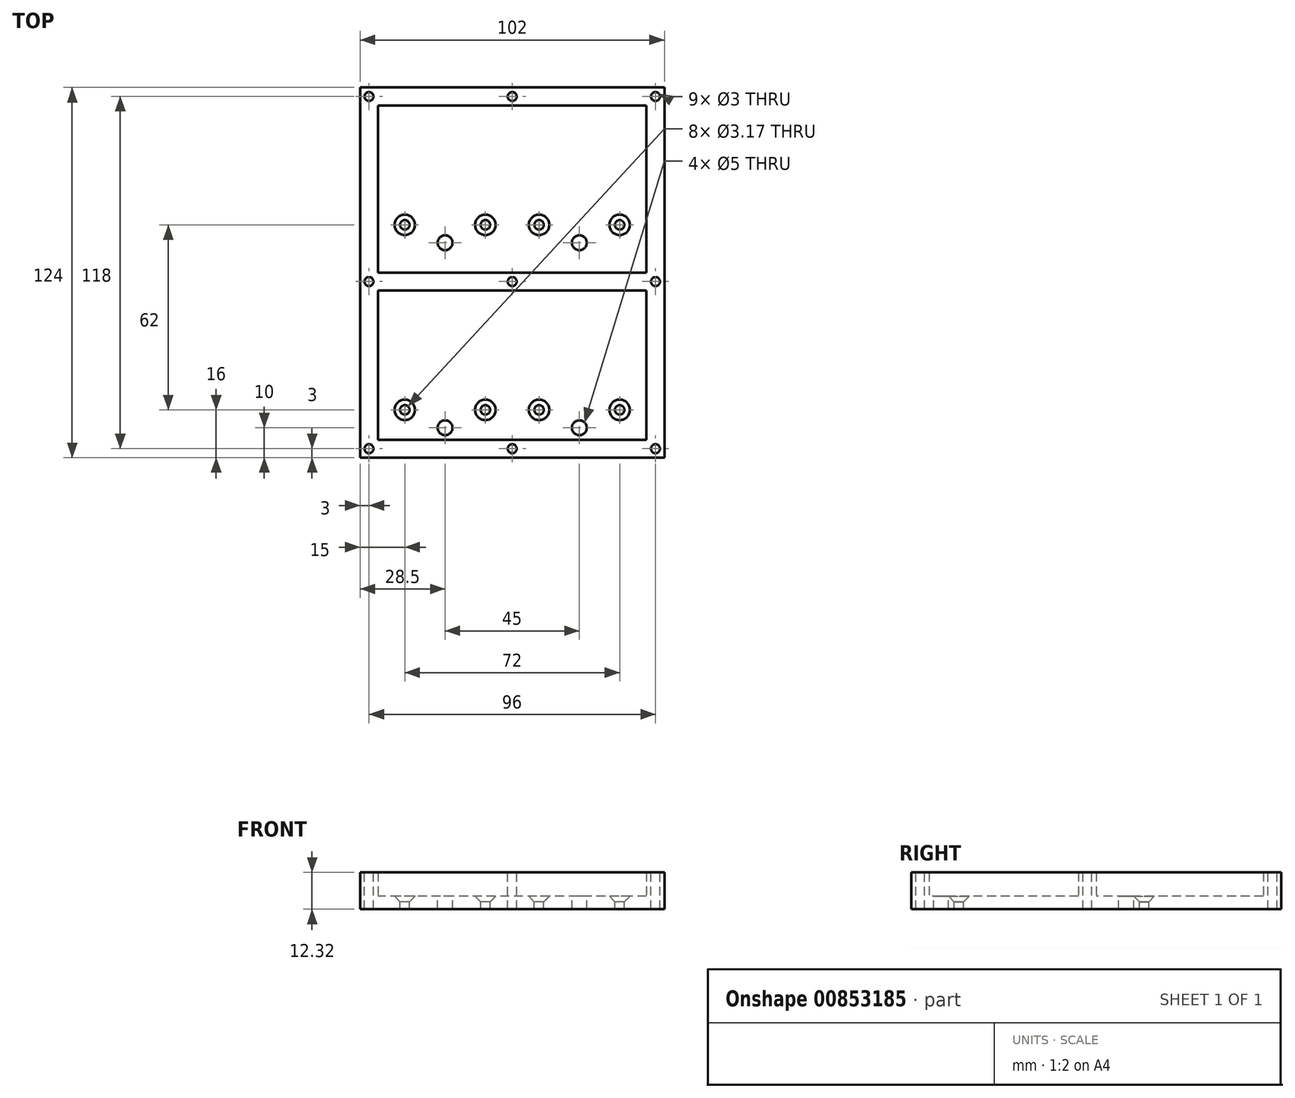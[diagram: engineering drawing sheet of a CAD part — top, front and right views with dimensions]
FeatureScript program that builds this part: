
annotation { "Feature Type Name" : "Feature", "Feature Type Description" : "" }
export const myFeature = defineFeature(function(context is Context, id is Id, definition is map)
    precondition{}
    {
        {
            var Q0;
            Q0=qCreatedBy(makeId("Top.planeOp"),FACE);
            var sketch = newSketch(context, id + "F0", { "sketchPlane" : qUnion([Q0])});
            skLineSegment(sketch, "E0.bottom", {"start": v(51, 62) * mm, "end": v(-51, 62) * mm});
            skLineSegment(sketch, "E0.top", {"start": v(51, -62) * mm, "end": v(-51, -62) * mm});
            skLineSegment(sketch, "E0.left", {"start": v(51, 62) * mm, "end": v(51, -62) * mm});
            skLineSegment(sketch, "E0.right", {"start": v(-51, 62) * mm, "end": v(-51, -62) * mm});
            skPoint(sketch, "E0.middle", {"position": v(0, 0) * mm});
            skSolve(sketch);
        }
        {
            var Q0;
            Q0 = qSketchRegion(id + "F0", true);
            extrude(context, id + "F1", {"entities" : qUnion([Q0]), "depth" : 4.32 * mm, "offsetDistance" : 25 * mm});
        }
        {
            var Q0;
            Q0=makeQuery(id+"F1.opExtrude","CAP_FACE",FACE,{"disambiguationData":[OSD([sQuery(id+"F0.wireOp",EDGE,"E0.bottom"),sQuery(id+"F0.wireOp",EDGE,"E0.top"),sQuery(id+"F0.wireOp",EDGE,"E0.left"),sQuery(id+"F0.wireOp",EDGE,"E0.right")])],"isStart":false});
            var sketch = newSketch(context, id + "F2", { "sketchPlane" : qUnion([Q0])});
            skLineSegment(sketch, "E1.bottom", {"start": v(45, 56) * mm, "end": v(-45, 56) * mm});
            skLineSegment(sketch, "E1.top", {"start": v(45, 29) * mm, "end": v(-45, 29) * mm});
            skLineSegment(sketch, "E1.left", {"start": v(45, 56) * mm, "end": v(45, 29) * mm});
            skLineSegment(sketch, "E1.right", {"start": v(-45, 56) * mm, "end": v(-45, 29) * mm});
            skPoint(sketch, "E1.middle", {"position": v(0, 42.5) * mm});
            skLineSegment(sketch, "E2.bottom", {"start": v(45, -6) * mm, "end": v(-45, -6) * mm});
            skLineSegment(sketch, "E2.top", {"start": v(45, -33) * mm, "end": v(-45, -33) * mm});
            skLineSegment(sketch, "E2.left", {"start": v(45, -6) * mm, "end": v(45, -33) * mm});
            skLineSegment(sketch, "E2.right", {"start": v(-45, -6) * mm, "end": v(-45, -33) * mm});
            skPoint(sketch, "E2.middle", {"position": v(0, -19.5) * mm});
            skLineSegment(sketch, "E3.bottom", {"start": v(51, 62) * mm, "end": v(-51, 62) * mm});
            skLineSegment(sketch, "E3.top", {"start": v(51, -62) * mm, "end": v(-51, -62) * mm});
            skLineSegment(sketch, "E3.left", {"start": v(51, 62) * mm, "end": v(51, -62) * mm});
            skLineSegment(sketch, "E3.right", {"start": v(-51, 62) * mm, "end": v(-51, -62) * mm});
            skPoint(sketch, "E3.middle", {"position": v(0, 0) * mm});
            skLineSegment(sketch, "E4.top", {"start": v(45, -56) * mm, "end": v(-45, -56) * mm});
            skLineSegment(sketch, "E4.left", {"start": v(45, 56) * mm, "end": v(45, -56) * mm});
            skLineSegment(sketch, "E4.right", {"start": v(-45, 56) * mm, "end": v(-45, -56) * mm});
            skPoint(sketch, "E5", {"position": v(-22.5, 10) * mm});
            skPoint(sketch, "E6", {"position": v(-9, 16) * mm});
            skPoint(sketch, "E7", {"position": v(-36, 16) * mm});
            skPoint(sketch, "E8", {"position": v(22.5, 10) * mm});
            skPoint(sketch, "E9", {"position": v(9, 16) * mm});
            skPoint(sketch, "E10", {"position": v(36, 16) * mm});
            skPoint(sketch, "E11", {"position": v(-22.5, -52) * mm});
            skPoint(sketch, "E12", {"position": v(22.5, -52) * mm});
            skPoint(sketch, "E13", {"position": v(-36, -46) * mm});
            skPoint(sketch, "E14", {"position": v(-9, -46) * mm});
            skPoint(sketch, "E15", {"position": v(36, -46) * mm});
            skPoint(sketch, "E16", {"position": v(9, -46) * mm});
            skLineSegment(sketch, "E17.bottom", {"start": v(45, 0) * mm, "end": v(-45, 0) * mm});
            skLineSegment(sketch, "E17.left", {"start": v(45, 0) * mm, "end": v(45, -6) * mm});
            skLineSegment(sketch, "E17.right", {"start": v(-45, 0) * mm, "end": v(-45, -6) * mm});
            skPoint(sketch, "E17.middle", {"position": v(0, -3) * mm});
            skSolve(sketch);
        }
        {
            var Q0;
            Q0=makeQuery(id+"F2.imprint","IMPRINT",FACE,{"disambiguationData":[TD([[makeQuery(id+"F2.imprint","IMPRINT",EDGE,{"derivedFrom":sQuery(id+"F2.wireOp",EDGE,"E3.bottom")}),1.0]])]});
            var Q1;
            Q1=makeQuery(id+"F2.imprint","IMPRINT",FACE,{"disambiguationData":[TD([[makeQuery(id+"F2.imprint","IMPRINT",EDGE,{"derivedFrom":sQuery(id+"F2.wireOp",EDGE,"E17.bottom")}),1.0]])]});
            extrude(context, id + "F3", {"entities" : qUnion([Q0, Q1]), "operationType" : NewBodyOperationType.ADD, "depth" : 8 * mm, "offsetDistance" : 25 * mm});
        }
        {
            var Q0;
            Q0=sQuery(id+"F2.wireOp",VERTEX,"E7");
            var Q1;
            Q1=sQuery(id+"F2.wireOp",VERTEX,"E6");
            var Q2;
            Q2=sQuery(id+"F2.wireOp",VERTEX,"E9");
            var Q3;
            Q3=sQuery(id+"F2.wireOp",VERTEX,"E10");
            var Q4;
            Q4=sQuery(id+"F2.wireOp",VERTEX,"E16");
            var Q5;
            Q5=sQuery(id+"F2.wireOp",VERTEX,"E15");
            var Q6;
            Q6=sQuery(id+"F2.wireOp",VERTEX,"E14");
            var Q7;
            Q7=sQuery(id+"F2.wireOp",VERTEX,"E13");
            var Q8;
            Q8=makeQuery(id+"F1.opExtrude","SWEPT_BODY",BODY,{"disambiguationData":[OSD([sQuery(id+"F0.wireOp",EDGE,"E0.bottom"),sQuery(id+"F0.wireOp",EDGE,"E0.top"),sQuery(id+"F0.wireOp",EDGE,"E0.left"),sQuery(id+"F0.wireOp",EDGE,"E0.right")])]});
            hole(context, id + "F4", {"style" : HoleStyle.C_SINK, "endStyle" : HoleEndStyle.THROUGH, "holeDiameter" : 3.17 * mm, "cSinkDiameter" : 6.86 * mm, "cSinkAngle" : 90 * degree, "majorDiameter" : 5 * mm, "isTappedThrough" : true, "tappedDepth" : 12 * mm, "tapClearance" : 3, "locations" : qUnion([Q0, Q1, Q2, Q3, Q4, Q5, Q6, Q7]), "scope" : qUnion([Q8])});
        }
        {
            var Q0;
            Q0=sQuery(id+"F2.wireOp",VERTEX,"E5");
            var Q1;
            Q1=sQuery(id+"F2.wireOp",VERTEX,"E8");
            var Q2;
            Q2=sQuery(id+"F2.wireOp",VERTEX,"E12");
            var Q3;
            Q3=sQuery(id+"F2.wireOp",VERTEX,"E11");
            var Q4;
            Q4=makeQuery(id+"F1.opExtrude","SWEPT_BODY",BODY,{"disambiguationData":[OSD([sQuery(id+"F0.wireOp",EDGE,"E0.bottom"),sQuery(id+"F0.wireOp",EDGE,"E0.top"),sQuery(id+"F0.wireOp",EDGE,"E0.left"),sQuery(id+"F0.wireOp",EDGE,"E0.right")])]});
            hole(context, id + "F5", {"style" : HoleStyle.SIMPLE, "endStyle" : HoleEndStyle.THROUGH, "holeDiameter" : 5 * mm, "majorDiameter" : 5 * mm, "isTappedThrough" : true, "tappedDepth" : 12 * mm, "tapClearance" : 3, "locations" : qUnion([Q0, Q1, Q2, Q3]), "scope" : qUnion([Q4])});
        }
        {
            var Q0;
            Q0=makeQuery(id+"F3.opExtrude","CAP_FACE",FACE,{"disambiguationData":[OSD([sQuery(id+"F2.wireOp",EDGE,"E3.bottom"),sQuery(id+"F2.wireOp",EDGE,"E3.top"),sQuery(id+"F2.wireOp",EDGE,"E3.left"),sQuery(id+"F2.wireOp",EDGE,"E3.right"),sQuery(id+"F2.wireOp",EDGE,"E1.bottom"),sQuery(id+"F2.wireOp",EDGE,"E4.top"),sQuery(id+"F2.wireOp",EDGE,"E4.left"),sQuery(id+"F2.wireOp",EDGE,"E4.right"),sQuery(id+"F2.wireOp",EDGE,"E17.bottom"),sQuery(id+"F2.wireOp",EDGE,"E2.bottom")])],"isStart":false});
            var sketch = newSketch(context, id + "F6", { "sketchPlane" : qUnion([Q0])});
            skPoint(sketch, "E18", {"position": v(-48, 59) * mm});
            skPoint(sketch, "E19", {"position": v(48, 59) * mm});
            skPoint(sketch, "E20", {"position": v(-48, -3) * mm});
            skPoint(sketch, "E21", {"position": v(-48, -59) * mm});
            skPoint(sketch, "E22", {"position": v(48, -3) * mm});
            skPoint(sketch, "E23", {"position": v(48, -59) * mm});
            skPoint(sketch, "E24", {"position": v(0, 59) * mm});
            skPoint(sketch, "E25", {"position": v(0, -3) * mm});
            skPoint(sketch, "E26", {"position": v(0, -59) * mm});
            skSolve(sketch);
        }
        {
            var Q0;
            Q0=sQuery(id+"F6.wireOp",VERTEX,"E18");
            var Q1;
            Q1=sQuery(id+"F6.wireOp",VERTEX,"E24");
            var Q2;
            Q2=sQuery(id+"F6.wireOp",VERTEX,"E19");
            var Q3;
            Q3=sQuery(id+"F6.wireOp",VERTEX,"E20");
            var Q4;
            Q4=sQuery(id+"F6.wireOp",VERTEX,"E22");
            var Q5;
            Q5=sQuery(id+"F6.wireOp",VERTEX,"E21");
            var Q6;
            Q6=sQuery(id+"F6.wireOp",VERTEX,"E26");
            var Q7;
            Q7=sQuery(id+"F6.wireOp",VERTEX,"E23");
            var Q8;
            Q8=sQuery(id+"F6.wireOp",VERTEX,"E25");
            var Q9;
            Q9=makeQuery(id+"F1.opExtrude","SWEPT_BODY",BODY,{"disambiguationData":[OSD([sQuery(id+"F0.wireOp",EDGE,"E0.bottom"),sQuery(id+"F0.wireOp",EDGE,"E0.top"),sQuery(id+"F0.wireOp",EDGE,"E0.left"),sQuery(id+"F0.wireOp",EDGE,"E0.right")])]});
            hole(context, id + "F7", {"style" : HoleStyle.SIMPLE, "endStyle" : HoleEndStyle.THROUGH, "holeDiameter" : 3 * mm, "majorDiameter" : 5 * mm, "isTappedThrough" : true, "tappedDepth" : 12 * mm, "tapClearance" : 3, "locations" : qUnion([Q0, Q1, Q2, Q3, Q4, Q5, Q6, Q7, Q8]), "scope" : qUnion([Q9])});
        }
    });
